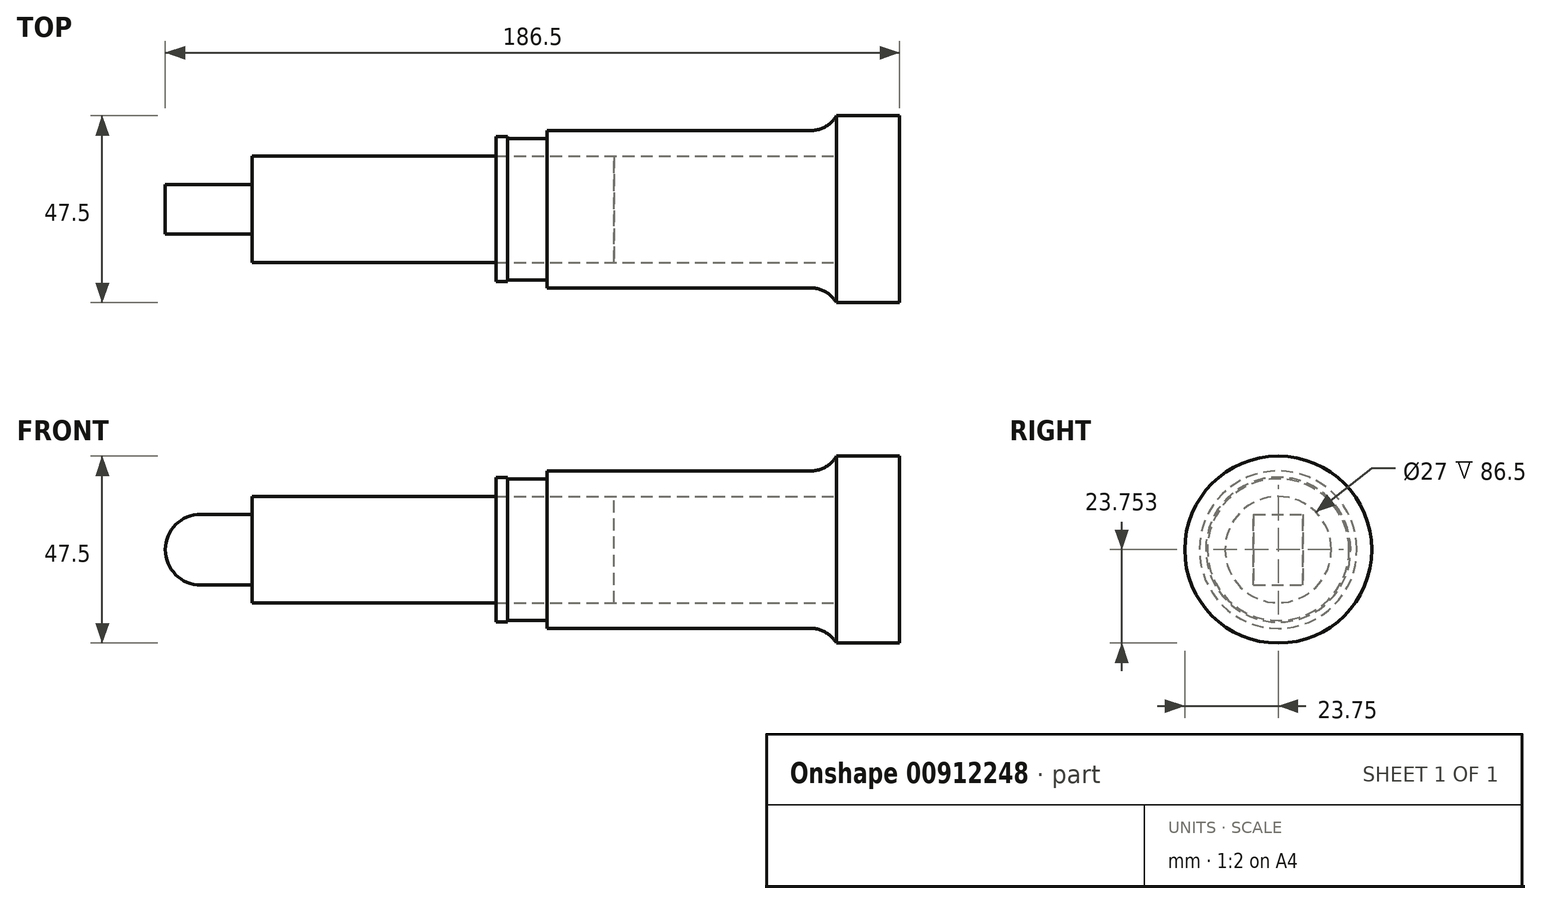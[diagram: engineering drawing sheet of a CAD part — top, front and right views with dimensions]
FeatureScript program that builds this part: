
annotation { "Feature Type Name" : "Feature", "Feature Type Description" : "" }
export const myFeature = defineFeature(function(context is Context, id is Id, definition is map)
    precondition{}
    {
        {
            var Q0;
            Q0=qCreatedBy(makeId("Front.planeOp"),FACE);
            var sketch = newSketch(context, id + "F0", { "sketchPlane" : qUnion([Q0])});
            skCircle(sketch, "E0", {"center": v(-89.07, -6.73) * mm, "radius": 9 * mm});
            skLineSegment(sketch, "E1", {"start": v(-89.07, -6.73) * mm, "end": v(110.93, -6.73) * mm, "construction": true});
            skCircle(sketch, "E2", {"center": v(110.93, -6.73) * mm, "radius": 9 * mm});
            skLineSegment(sketch, "E3", {"start": v(-14.07, -6.73) * mm, "end": v(-14.07, 11.67) * mm});
            skLineSegment(sketch, "E4", {"start": v(-14.07, 11.67) * mm, "end": v(-11.07, 11.67) * mm});
            skLineSegment(sketch, "E5", {"start": v(-11.07, 11.67) * mm, "end": v(-11.07, 11.27) * mm});
            skLineSegment(sketch, "E6", {"start": v(-11.07, 11.27) * mm, "end": v(-1.07, 11.27) * mm});
            skLineSegment(sketch, "E7", {"start": v(-1.07, 11.27) * mm, "end": v(-1.07, 13.27) * mm});
            skLineSegment(sketch, "E8", {"start": v(-1.07, 13.27) * mm, "end": v(65.93, 13.27) * mm});
            skLineSegment(sketch, "E9", {"start": v(88.43, -6.73) * mm, "end": v(88.43, 17.02) * mm});
            skLineSegment(sketch, "E10", {"start": v(88.43, 17.02) * mm, "end": v(72.43, 17.02) * mm});
            skArc(sketch, "E11", {"start": v(65.93, 13.27) * mm, "mid": v(69.68, 14.28) * mm, "end": v(72.43, 17.02) * mm});
            skLineSegment(sketch, "E12", {"start": v(-14.07, -6.73) * mm, "end": v(88.43, -6.73) * mm});
            skLineSegment(sketch, "E13.bottom", {"start": v(-14.07, -6.73) * mm, "end": v(-76.07, -6.73) * mm});
            skLineSegment(sketch, "E13.top", {"start": v(-14.07, 6.77) * mm, "end": v(-76.07, 6.77) * mm});
            skLineSegment(sketch, "E13.left", {"start": v(-14.07, -6.73) * mm, "end": v(-14.07, 6.77) * mm});
            skLineSegment(sketch, "E13.right", {"start": v(-76.07, -6.73) * mm, "end": v(-76.07, 6.77) * mm});
            skLineSegment(sketch, "E14", {"start": v(-89.07, 2.27) * mm, "end": v(-76.07, 2.27) * mm});
            skLineSegment(sketch, "E15", {"start": v(-76.07, -6.73) * mm, "end": v(-89.07, -6.73) * mm});
            skLineSegment(sketch, "E16", {"start": v(-89.07, -6.73) * mm, "end": v(-89.07, 2.27) * mm});
            skLineSegment(sketch, "E17.bottom", {"start": v(-14.07, 6.77) * mm, "end": v(15.93, 6.77) * mm});
            skLineSegment(sketch, "E17.top", {"start": v(-14.07, -6.73) * mm, "end": v(15.93, -6.73) * mm});
            skLineSegment(sketch, "E17.left", {"start": v(-14.07, 6.77) * mm, "end": v(-14.07, -6.73) * mm});
            skLineSegment(sketch, "E17.right", {"start": v(15.93, 6.77) * mm, "end": v(15.93, -6.73) * mm});
            skLineSegment(sketch, "E18.bottom", {"start": v(-89.07, -15.73) * mm, "end": v(-76.07, -15.73) * mm});
            skLineSegment(sketch, "E18.top", {"start": v(-89.07, -6.73) * mm, "end": v(-76.07, -6.73) * mm});
            skLineSegment(sketch, "E18.left", {"start": v(-89.07, -15.73) * mm, "end": v(-89.07, -6.73) * mm});
            skLineSegment(sketch, "E18.right", {"start": v(-76.07, -15.73) * mm, "end": v(-76.07, -6.73) * mm});
            skLineSegment(sketch, "E19.bottom", {"start": v(15.93, 6.77) * mm, "end": v(72.43, 6.77) * mm});
            skLineSegment(sketch, "E19.top", {"start": v(15.93, -6.73) * mm, "end": v(72.43, -6.73) * mm});
            skLineSegment(sketch, "E19.right", {"start": v(72.43, 6.77) * mm, "end": v(72.43, -6.73) * mm});
            skLineSegment(sketch, "E20", {"start": v(88.43, -6.73) * mm, "end": v(88.43, -15.73) * mm});
            skLineSegment(sketch, "E21", {"start": v(110.93, -15.73) * mm, "end": v(88.43, -15.73) * mm});
            skArc(sketch, "E22", {"start": v(88.43, 11.27) * mm, "mid": v(100.13, 5.64) * mm, "end": v(112.62, 2.11) * mm});
            skSolve(sketch);
        }
        {
            var Q0;
            {var subQ6=sQuery(id+"F0.wireOp",EDGE,"E4");Q0=makeQuery(id+"F0.imprint","IMPRINT",FACE,{"disambiguationData":[TD([[makeQuery(id+"F0.imprint","IMPRINT",EDGE,{"derivedFrom":subQ6}),-1.0]])]});}
            var Q1;
            Q1=sQuery(id+"F0.wireOp",EDGE,"E13.bottom");
            revolve(context, id + "F1", {"surfaceOperationType" : NewSurfaceOperationType.NEW, "entities" : qUnion([Q0]), "axis" : qUnion([Q1]), "revolveType" : RevolveType.FULL});
        }
        {
            var Q0;
            {var subQ1=sQuery(id+"F0.wireOp",EDGE,"E13.bottom");Q0=makeQuery(id+"F0.imprint","IMPRINT",FACE,{"disambiguationData":[TD([[makeQuery(id+"F0.imprint","IMPRINT",EDGE,{"derivedFrom":subQ1}),-1.0]])]});}
            var Q1;
            {var subQ3=sQuery(id+"F0.wireOp",EDGE,"E17.bottom");Q1=makeQuery(id+"F0.imprint","IMPRINT",FACE,{"disambiguationData":[TD([[makeQuery(id+"F0.imprint","IMPRINT",EDGE,{"derivedFrom":subQ3}),-1.0]])]});}
            var Q2;
            Q2=sQuery(id+"F0.wireOp",EDGE,"E13.bottom");
            revolve(context, id + "F2", {"surfaceOperationType" : NewSurfaceOperationType.NEW, "entities" : qUnion([Q0, Q1]), "axis" : qUnion([Q2]), "revolveType" : RevolveType.FULL});
        }
        {
            var Q0;
            {var subQ0=sQuery(id+"F0.wireOp",EDGE,"E16");Q0=makeQuery(id+"F0.imprint","IMPRINT",FACE,{"disambiguationData":[TD([[makeQuery(id+"F0.imprint","IMPRINT",EDGE,{"derivedFrom":subQ0}),-1.0]])]});}
            var Q1;
            {var subQ0=sQuery(id+"F0.wireOp",EDGE,"E14");Q1=makeQuery(id+"F0.imprint","IMPRINT",FACE,{"disambiguationData":[TD([[makeQuery(id+"F0.imprint","IMPRINT",EDGE,{"derivedFrom":subQ0}),-1.0]])]});}
            var Q2;
            {var subQ3=sQuery(id+"F0.wireOp",EDGE,"E18.bottom");Q2=makeQuery(id+"F0.imprint","IMPRINT",FACE,{"disambiguationData":[TD([[makeQuery(id+"F0.imprint","IMPRINT",EDGE,{"derivedFrom":subQ3}),1.0]])]});}
            var Q3;
            {var subQ3=sQuery(id+"F0.wireOp",EDGE,"E18.left");Q3=makeQuery(id+"F0.imprint","IMPRINT",FACE,{"disambiguationData":[TD([[makeQuery(id+"F0.imprint","IMPRINT",EDGE,{"derivedFrom":subQ3}),-1.0]])]});}
            var Q4;
            {var subQ0=sQuery(id+"F0.wireOp",EDGE,"E16");Q4=makeQuery(id+"F0.imprint","IMPRINT",FACE,{"disambiguationData":[TD([[makeQuery(id+"F0.imprint","IMPRINT",EDGE,{"derivedFrom":subQ0}),1.0]])]});}
            extrude(context, id + "F3", {"entities" : qUnion([Q0, Q1, Q2, Q3, Q4]), "operationType" : NewBodyOperationType.ADD, "endBound" : BoundingType.SYMMETRIC, "depth" : 12.5 * mm, "offsetDistance" : 25 * mm});
        }
    });
